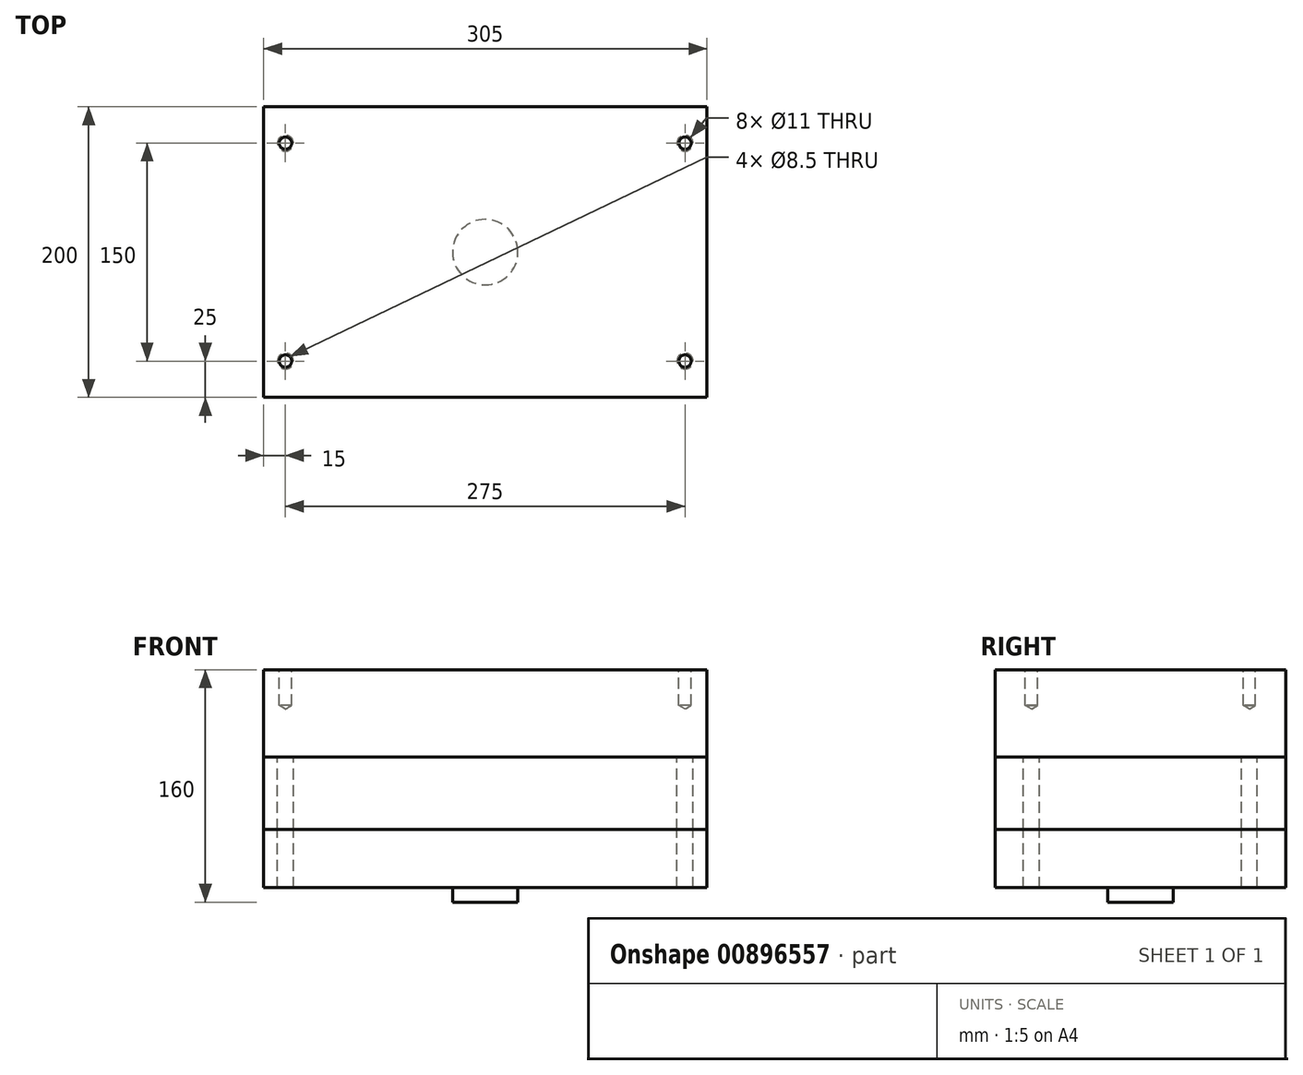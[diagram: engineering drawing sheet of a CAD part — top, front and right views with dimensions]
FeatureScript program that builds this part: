
annotation { "Feature Type Name" : "Feature", "Feature Type Description" : "" }
export const myFeature = defineFeature(function(context is Context, id is Id, definition is map)
    precondition{}
    {
        {
            assignVariable(context, id + "F0", {"name" : "Max", "anyValue" : 150});
        }
        {
            assignVariable(context, id + "F1", {"name" : "Top", "anyValue" : 60});
        }
        {
            assignVariable(context, id + "F2", {"name" : "Base", "anyValue" : 40});
        }
        {
            var Q0;
            Q0=qCreatedBy(makeId("Top.planeOp"),FACE);
            var sketch = newSketch(context, id + "F3", { "sketchPlane" : qUnion([Q0])});
            skLineSegment(sketch, "E0.bottom", {"start": v(-152.5, 100) * mm, "end": v(152.5, 100) * mm});
            skLineSegment(sketch, "E0.top", {"start": v(-152.5, -100) * mm, "end": v(152.5, -100) * mm});
            skLineSegment(sketch, "E0.left", {"start": v(-152.5, 100) * mm, "end": v(-152.5, -100) * mm});
            skLineSegment(sketch, "E0.right", {"start": v(152.5, 100) * mm, "end": v(152.5, -100) * mm});
            skPoint(sketch, "E0.middle", {"position": v(0, 0) * mm});
            skSolve(sketch);
        }
        {
            var Q0;
            Q0=makeQuery(id+"F3.imprint","IMPRINT",FACE,{"disambiguationData":[TD([[makeQuery(id+"F3.imprint","IMPRINT",EDGE,{"derivedFrom":sQuery(id+"F3.wireOp",EDGE,"E0.bottom")}),-1.0]])]});
            extrude(context, id + "F4", {"entities" : qUnion([Q0]), "depth" : (getVariable(context, 'Top')) * mm, "offsetDistance" : 25 * mm});
        }
        {
            var Q0;
            Q0=makeQuery(id+"F4.opExtrude","CAP_FACE",FACE,{"disambiguationData":[OSD([sQuery(id+"F3.wireOp",EDGE,"E0.bottom"),sQuery(id+"F3.wireOp",EDGE,"E0.top"),sQuery(id+"F3.wireOp",EDGE,"E0.left"),sQuery(id+"F3.wireOp",EDGE,"E0.right")])],"isStart":false});
            var sketch = newSketch(context, id + "F5", { "sketchPlane" : qUnion([Q0])});
            skLineSegment(sketch, "E1.bottom", {"start": v(-137.5, 75) * mm, "end": v(137.5, 75) * mm, "construction": true});
            skLineSegment(sketch, "E1.top", {"start": v(-137.5, -75) * mm, "end": v(137.5, -75) * mm, "construction": true});
            skLineSegment(sketch, "E1.left", {"start": v(-137.5, 75) * mm, "end": v(-137.5, -75) * mm, "construction": true});
            skLineSegment(sketch, "E1.right", {"start": v(137.5, 75) * mm, "end": v(137.5, -75) * mm, "construction": true});
            skPoint(sketch, "E1.middle", {"position": v(0, 0) * mm});
            skSolve(sketch);
        }
        {
            var Q0;
            Q0=sQuery(id+"F5.wireOp",VERTEX,"E1.bottom.start");
            var Q1;
            Q1=sQuery(id+"F5.wireOp",VERTEX,"E1.bottom.end");
            var Q2;
            Q2=sQuery(id+"F5.wireOp",VERTEX,"E1.top.start");
            var Q3;
            Q3=sQuery(id+"F5.wireOp",VERTEX,"E1.top.end");
            var Q4;
            Q4=makeQuery(id+"F4.opExtrude","SWEPT_BODY",BODY,{"disambiguationData":[OSD([sQuery(id+"F3.wireOp",EDGE,"E0.bottom"),sQuery(id+"F3.wireOp",EDGE,"E0.top"),sQuery(id+"F3.wireOp",EDGE,"E0.left"),sQuery(id+"F3.wireOp",EDGE,"E0.right")])]});
            hole(context, id + "F6", {"style" : HoleStyle.SIMPLE, "endStyle" : HoleEndStyle.BLIND, "standardTappedOrClearance" : lookupTablePath({ "standard" : "ISO", "engagement" : "75%", "pitch" : "1.5 mm", "size" : "M10", "type" : "Tapped" }), "standardBlindInLast" : lookupTablePath({ "standard" : "ISO", "engagement" : "75%", "pitch" : "1.5 mm", "size" : "M10", "type" : "Tapped" }), "holeDiameter" : 8.5 * mm, "majorDiameter" : 10 * mm, "showTappedDepth" : true, "holeDepth" : 24.5 * mm, "tappedDepth" : 20 * mm, "tapClearance" : 3, "locations" : qUnion([Q0, Q1, Q2, Q3]), "scope" : qUnion([Q4])});
        }
        {
            var Q0;
            Q0 = qSketchRegion(id + "F3", true);
            extrude(context, id + "F7", {"entities" : qUnion([Q0]), "oppositeDirection" : true, "depth" : (getVariable(context, 'Max') - (getVariable(context, 'Top') + getVariable(context, 'Base'))) * mm, "offsetDistance" : 25 * mm});
        }
        {
            var Q0;
            Q0=makeQuery(id+"F7.opExtrude","CAP_FACE",FACE,{"disambiguationData":[OSD([sQuery(id+"F3.wireOp",EDGE,"E0.bottom"),sQuery(id+"F3.wireOp",EDGE,"E0.top"),sQuery(id+"F3.wireOp",EDGE,"E0.left"),sQuery(id+"F3.wireOp",EDGE,"E0.right")])],"isStart":false});
            extrude(context, id + "F8", {"entities" : qUnion([Q0]), "depth" : (getVariable(context, 'Base')) * mm, "offsetDistance" : 25 * mm});
        }
        {
            var Q0;
            Q0=makeQuery(id+"F8.opExtrude","CAP_FACE",FACE,{"disambiguationData":[OSD([sQuery(id+"F3.wireOp",EDGE,"E0.bottom"),sQuery(id+"F3.wireOp",EDGE,"E0.top"),sQuery(id+"F3.wireOp",EDGE,"E0.left"),sQuery(id+"F3.wireOp",EDGE,"E0.right")])],"isStart":false});
            var sketch = newSketch(context, id + "F9", { "sketchPlane" : qUnion([Q0])});
            skCircle(sketch, "E2", {"center": v(0, 0) * mm, "radius": 22.5 * mm});
            skSolve(sketch);
        }
        {
            var Q0;
            Q0=makeQuery(id+"F9.imprint","IMPRINT",FACE,{"disambiguationData":[TD([[makeQuery(id+"F9.imprint","IMPRINT",EDGE,{"derivedFrom":sQuery(id+"F9.wireOp",EDGE,"E2")}),1.0]])]});
            extrude(context, id + "F10", {"entities" : qUnion([Q0]), "operationType" : NewBodyOperationType.ADD, "depth" : 10 * mm, "offsetDistance" : 25 * mm});
        }
        {
            var Q0;
            Q0=qCreatedBy(makeId("Top.planeOp"),FACE);
            var sketch = newSketch(context, id + "F11", { "sketchPlane" : qUnion([Q0])});
            skPoint(sketch, "E3", {"position": v(-137.5, -75) * mm});
            skPoint(sketch, "E4", {"position": v(137.5, -75) * mm});
            skPoint(sketch, "E5", {"position": v(137.5, 75) * mm});
            skPoint(sketch, "E6", {"position": v(-137.5, 75) * mm});
            skSolve(sketch);
        }
        {
            var Q0;
            Q0=sQuery(id+"F11.wireOp",VERTEX,"E3");
            var Q1;
            Q1=sQuery(id+"F11.wireOp",VERTEX,"E6");
            var Q2;
            Q2=sQuery(id+"F11.wireOp",VERTEX,"E5");
            var Q3;
            Q3=sQuery(id+"F11.wireOp",VERTEX,"E4");
            var Q4;
            Q4=makeQuery(id+"F7.opExtrude","SWEPT_BODY",BODY,{"disambiguationData":[OSD([sQuery(id+"F3.wireOp",EDGE,"E0.bottom"),sQuery(id+"F3.wireOp",EDGE,"E0.top"),sQuery(id+"F3.wireOp",EDGE,"E0.left"),sQuery(id+"F3.wireOp",EDGE,"E0.right")])]});
            var Q5;
            Q5=makeQuery(id+"F8.opExtrude","SWEPT_BODY",BODY,{"disambiguationData":[OSD([sQuery(id+"F3.wireOp",EDGE,"E0.bottom"),sQuery(id+"F3.wireOp",EDGE,"E0.top"),sQuery(id+"F3.wireOp",EDGE,"E0.left"),sQuery(id+"F3.wireOp",EDGE,"E0.right")])]});
            hole(context, id + "F12", {"style" : HoleStyle.SIMPLE, "endStyle" : HoleEndStyle.THROUGH, "holeDiameter" : 11 * mm, "majorDiameter" : 10 * mm, "tappedDepth" : 20 * mm, "tapClearance" : 3, "locations" : qUnion([Q0, Q1, Q2, Q3]), "scope" : qUnion([Q4, Q5])});
        }
    });
